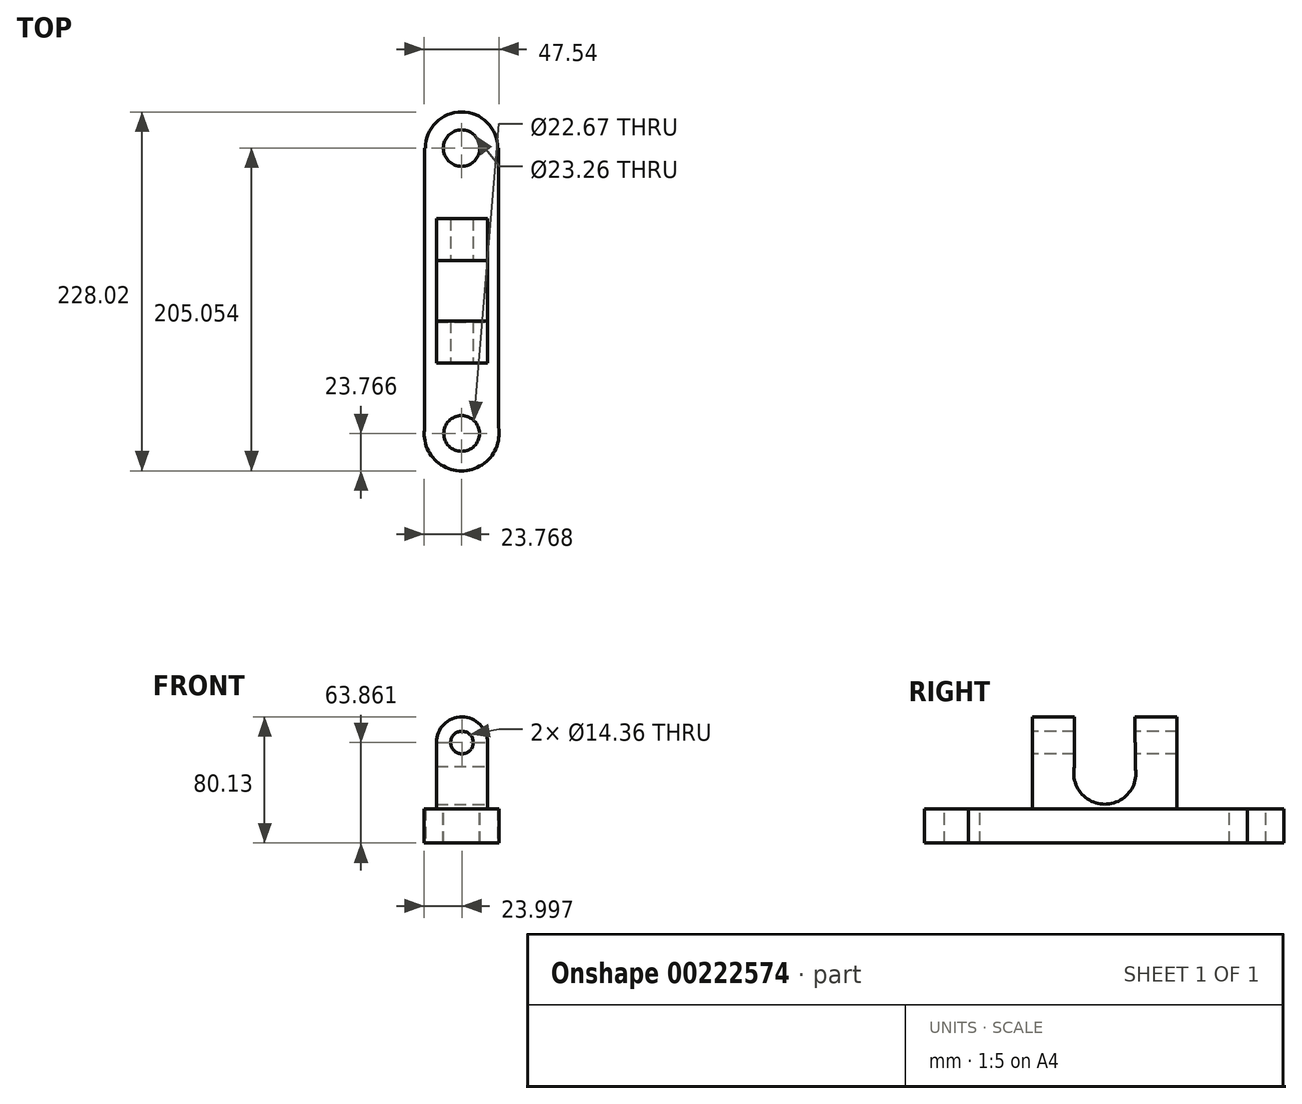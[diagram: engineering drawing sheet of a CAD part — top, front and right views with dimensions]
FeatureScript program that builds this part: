
annotation { "Feature Type Name" : "Feature", "Feature Type Description" : "" }
export const myFeature = defineFeature(function(context is Context, id is Id, definition is map)
    precondition{}
    {
        {
            var Q0;
            Q0=qCreatedBy(makeId("Top.planeOp"),FACE);
            var sketch = newSketch(context, id + "F0", { "sketchPlane" : qUnion([Q0])});
            skLineSegment(sketch, "E0.bottom", {"start": v(0, 90.64) * mm, "end": v(-46.82, 90.64) * mm});
            skLineSegment(sketch, "E0.top", {"start": v(0, -90.64) * mm, "end": v(-46.82, -90.64) * mm});
            skLineSegment(sketch, "E0.left", {"start": v(0, 90.64) * mm, "end": v(0, -90.64) * mm});
            skLineSegment(sketch, "E0.right", {"start": v(-46.82, 90.64) * mm, "end": v(-46.82, -90.64) * mm});
            skPoint(sketch, "E0.middle", {"position": v(-23.41, 0) * mm});
            skCircle(sketch, "E1", {"center": v(-23.41, -90.64) * mm, "radius": 23.77 * mm});
            skCircle(sketch, "E2", {"center": v(-23.41, 90.64) * mm, "radius": 22.96 * mm});
            skSolve(sketch);
        }
        {
            var Q0;
            {var subQ0=sQuery(id+"F0.wireOp",EDGE,"E2");var subQ1=sQuery(id+"F0.wireOp",EDGE,"E0.bottom");var subQ2=makeQuery(id+"F0.imprint","INTERSECT",VERTEX,{"disambiguationData":[OD(0.0)],"derivedFrom":[subQ1,subQ0]});Q0=makeQuery(id+"F0.imprint","IMPRINT",FACE,{"disambiguationData":[TD([[makeQuery(id+"F0.imprint","IMPRINT",EDGE,{"disambiguationData":[TD([[subQ2,-1.0]])],"derivedFrom":subQ1}),-1.0]])]});}
            var Q1;
            {var subQ0=sQuery(id+"F0.wireOp",EDGE,"E2");var subQ1=sQuery(id+"F0.wireOp",EDGE,"E0.bottom");var subQ2=makeQuery(id+"F0.imprint","INTERSECT",VERTEX,{"disambiguationData":[OD(0.0)],"derivedFrom":[subQ1,subQ0]});Q1=makeQuery(id+"F0.imprint","IMPRINT",FACE,{"disambiguationData":[TD([[makeQuery(id+"F0.imprint","IMPRINT",EDGE,{"disambiguationData":[TD([[subQ2,-1.0]])],"derivedFrom":subQ1}),1.0]])]});}
            var Q2;
            {var subQ1=sQuery(id+"F0.wireOp",EDGE,"E0.bottom");var subQ5=sQuery(id+"F0.wireOp",EDGE,"E0.left");var subQ6=makeQuery(id+"F0.imprint","INTERSECT",VERTEX,{"derivedFrom":[subQ1,subQ5]});Q2=makeQuery(id+"F0.imprint","IMPRINT",FACE,{"disambiguationData":[TD([[makeQuery(id+"F0.imprint","IMPRINT",EDGE,{"disambiguationData":[TD([[subQ6,-1.0]])],"derivedFrom":subQ1}),1.0]])]});}
            var Q3;
            {var subQ0=sQuery(id+"F0.wireOp",EDGE,"E0.top");Q3=makeQuery(id+"F0.imprint","IMPRINT",FACE,{"disambiguationData":[TD([[makeQuery(id+"F0.imprint","IMPRINT",EDGE,{"derivedFrom":subQ0}),-1.0]])]});}
            var Q4;
            {var subQ0=sQuery(id+"F0.wireOp",EDGE,"E0.top");Q4=makeQuery(id+"F0.imprint","IMPRINT",FACE,{"disambiguationData":[TD([[makeQuery(id+"F0.imprint","IMPRINT",EDGE,{"derivedFrom":subQ0}),1.0]])]});}
            extrude(context, id + "F1", {"entities" : qUnion([Q0, Q1, Q2, Q3, Q4]), "depth" : 21.83 * mm});
        }
        {
            var Q0;
            Q0=makeQuery(id+"F1.opExtrude","CAP_FACE",FACE,{"disambiguationData":[OSD([sQuery(id+"F0.wireOp",EDGE,"E0.bottom"),sQuery(id+"F0.wireOp",EDGE,"E0.left"),sQuery(id+"F0.wireOp",EDGE,"E0.right"),sQuery(id+"F0.wireOp",EDGE,"E1"),sQuery(id+"F0.wireOp",EDGE,"E2")])],"isStart":false});
            var sketch = newSketch(context, id + "F2", { "sketchPlane" : qUnion([Q0])});
            skCircle(sketch, "E3", {"center": v(-23.41, -90.64) * mm, "radius": 11.34 * mm});
            skCircle(sketch, "E4", {"center": v(-23.41, 90.64) * mm, "radius": 11.63 * mm});
            skSolve(sketch);
        }
        {
            var Q0;
            Q0=makeQuery(id+"F2.imprint","IMPRINT",FACE,{"disambiguationData":[TD([[makeQuery(id+"F2.imprint","IMPRINT",EDGE,{"derivedFrom":sQuery(id+"F2.wireOp",EDGE,"E4")}),1.0]])]});
            var Q1;
            Q1=makeQuery(id+"F2.imprint","IMPRINT",FACE,{"disambiguationData":[TD([[makeQuery(id+"F2.imprint","IMPRINT",EDGE,{"derivedFrom":sQuery(id+"F2.wireOp",EDGE,"E3")}),1.0]])]});
            extrude(context, id + "F3", {"entities" : qUnion([Q0, Q1]), "operationType" : NewBodyOperationType.REMOVE, "endBound" : BoundingType.THROUGH_ALL, "oppositeDirection" : true, "depth" : 25.4 * mm});
        }
        {
            var Q0;
            Q0=makeQuery(id+"F1.opExtrude","CAP_FACE",FACE,{"disambiguationData":[OSD([sQuery(id+"F0.wireOp",EDGE,"E0.bottom"),sQuery(id+"F0.wireOp",EDGE,"E0.left"),sQuery(id+"F0.wireOp",EDGE,"E0.right"),sQuery(id+"F0.wireOp",EDGE,"E1"),sQuery(id+"F0.wireOp",EDGE,"E2")])],"isStart":false});
            var sketch = newSketch(context, id + "F4", { "sketchPlane" : qUnion([Q0])});
            skLineSegment(sketch, "E5.bottom", {"start": v(-6.91, -45.85) * mm, "end": v(-39.45, -45.85) * mm});
            skLineSegment(sketch, "E5.top", {"start": v(-6.91, 45.85) * mm, "end": v(-39.45, 45.85) * mm});
            skLineSegment(sketch, "E5.left", {"start": v(-6.91, -45.85) * mm, "end": v(-6.91, 45.85) * mm});
            skLineSegment(sketch, "E5.right", {"start": v(-39.45, -45.85) * mm, "end": v(-39.45, 45.85) * mm});
            skPoint(sketch, "E5.middle", {"position": v(-23.18, 0) * mm});
            skSolve(sketch);
        }
        {
            var Q0;
            Q0 = qSketchRegion(id + "F4", true);
            extrude(context, id + "F5", {"entities" : qUnion([Q0]), "operationType" : NewBodyOperationType.ADD, "depth" : 42.03 * mm});
        }
        {
            var Q0;
            Q0=makeQuery(id+"F5.opExtrude","SWEPT_FACE",FACE,{"disambiguationData":[OSD([sQuery(id+"F4.wireOp",EDGE,"E5.left")])]});
            var sketch = newSketch(context, id + "F6", { "sketchPlane" : qUnion([Q0])});
            skLineSegment(sketch, "E6.bottom", {"start": v(-19.28, 63.86) * mm, "end": v(19.33, 63.86) * mm});
            skLineSegment(sketch, "E6.top", {"start": v(-19.28, 44.4) * mm, "end": v(19.33, 44.4) * mm});
            skLineSegment(sketch, "E6.left", {"start": v(-19.28, 63.86) * mm, "end": v(-19.28, 44.4) * mm});
            skLineSegment(sketch, "E6.right", {"start": v(19.33, 63.86) * mm, "end": v(19.33, 44.4) * mm});
            skCircle(sketch, "E7", {"center": v(0.03, 44.4) * mm, "radius": 19.75 * mm});
            skSolve(sketch);
        }
        {
            var Q0;
            Q0 = qSketchRegion(id + "F6", true);
            extrude(context, id + "F7", {"entities" : qUnion([Q0]), "operationType" : NewBodyOperationType.REMOVE, "endBound" : BoundingType.THROUGH_ALL, "oppositeDirection" : true, "depth" : 25.4 * mm});
        }
        {
            var Q0;
            Q0=makeQuery(id+"F5.opExtrude","SWEPT_FACE",FACE,{"disambiguationData":[OSD([sQuery(id+"F4.wireOp",EDGE,"E5.bottom")])]});
            var sketch = newSketch(context, id + "F8", { "sketchPlane" : qUnion([Q0])});
            skArc(sketch, "E8", {"start": v(-6.91, 63.86) * mm, "mid": v(-23.18, 80.13) * mm, "end": v(-39.45, 63.86) * mm});
            skSolve(sketch);
        }
        {
            var Q0;
            Q0=makeQuery(id+"F5.opExtrude","SWEPT_FACE",FACE,{"disambiguationData":[OSD([sQuery(id+"F4.wireOp",EDGE,"E5.top")])]});
            var sketch = newSketch(context, id + "F9", { "sketchPlane" : qUnion([Q0])});
            skArc(sketch, "E9", {"start": v(39.45, 63.86) * mm, "mid": v(23.18, 80.13) * mm, "end": v(6.91, 63.86) * mm});
            skSolve(sketch);
        }
        {
            var Q0;
            Q0=makeQuery(id+"F9.imprint","IMPRINT",FACE,{"disambiguationData":[TD([[makeQuery(id+"F9.imprint","IMPRINT",EDGE,{"derivedFrom":sQuery(id+"F9.wireOp",EDGE,"E9")}),1.0]])]});
            extrude(context, id + "F10", {"entities" : qUnion([Q0]), "operationType" : NewBodyOperationType.ADD, "oppositeDirection" : true, "depth" : 26.6 * mm});
        }
        {
            var Q0;
            Q0=makeQuery(id+"F8.imprint","IMPRINT",FACE,{"disambiguationData":[TD([[makeQuery(id+"F8.imprint","IMPRINT",EDGE,{"derivedFrom":sQuery(id+"F8.wireOp",EDGE,"E8")}),1.0]])]});
            extrude(context, id + "F11", {"entities" : qUnion([Q0]), "operationType" : NewBodyOperationType.ADD, "oppositeDirection" : true, "depth" : 26.57 * mm});
        }
        {
            var Q0;
            {var subQ0=sQuery(id+"F4.wireOp",EDGE,"E5.bottom");Q0=makeQuery(id+"F11.boolean.opBoolean","MERGE",FACE,{"derivedFrom":[makeQuery(id+"F5.opExtrude","SWEPT_FACE",FACE,{"disambiguationData":[OSD([subQ0])]}),makeQuery(id+"F11.opExtrude","CAP_FACE",FACE,{"disambiguationData":[OSD([subQ0,sQuery(id+"F8.wireOp",EDGE,"E8")])],"isStart":true})]});}
            var sketch = newSketch(context, id + "F12", { "sketchPlane" : qUnion([Q0])});
            skCircle(sketch, "E10", {"center": v(-23.18, 63.86) * mm, "radius": 7.18 * mm});
            skSolve(sketch);
        }
        {
            var Q0;
            Q0=makeQuery(id+"F12.imprint","IMPRINT",FACE,{"disambiguationData":[TD([[makeQuery(id+"F12.imprint","IMPRINT",EDGE,{"derivedFrom":sQuery(id+"F12.wireOp",EDGE,"E10")}),1.0]])]});
            extrude(context, id + "F13", {"entities" : qUnion([Q0]), "operationType" : NewBodyOperationType.REMOVE, "endBound" : BoundingType.THROUGH_ALL, "oppositeDirection" : true, "depth" : 25.4 * mm});
        }
    });
